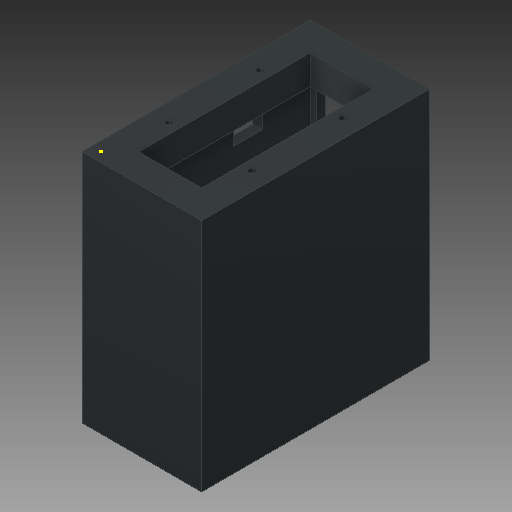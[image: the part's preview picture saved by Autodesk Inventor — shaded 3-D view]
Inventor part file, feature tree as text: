
AUTODESK INVENTOR PART (.ipt)
format: ipt  version: 2018 (Build 220112000, 112)  size: 163,328 bytes
history: native  units: mm
features: sketch x6, extrude x5
ambient origin geometry x8: Origin, YZ Plane, XZ Plane, XY Plane, X Axis, Y Axis, Z Axis, Center Point
bodies: Solid1 (feature_tree)
feature tree (11):
  extrude  "Extrusion1"  Depth=520.0mm
  extrude  "Extrusion2"  Depth=583.0mm TaperAngle=0.0deg
  extrude  "Extrusion3"  Depth=440.0mm
  sketch  "Sketch4"  dims[d7=77.0mm d8=38.0mm]
  extrude  "Extrusion4"  Depth=38.0mm
  extrude  "Extrusion5"  Depth=70.0mm
  sketch  "Sketch1"  dims[d0=250.0mm d1=520.0mm]
  sketch  "Sketch2"  dims[d2=23.0mm d3=583.0mm d4=0.0mm]
  sketch  "Sketch3"  dims[d5=220.0mm d6=440.0mm]
  sketch  "Sketch5"  dims[d9=583.0mm d10=0.0mm d11=70.0mm]
  sketch  "Sketch6"  dims[d12=80.0mm d13=430.0mm d14=143.0mm d15=583.0mm d16=0.0mm d17=47.0mm d18=583.0mm d19=0.0mm d20=16.0mm d21=170.0mm d22=45.0mm d23=16.0mm d24=170.0mm d25=45.0mm d26=10.0mm d27=0.0mm]
